# Revit family: Lighting-StreetLighting-GEWISS-STREET[O3]-WALL_BRACKET
name_source: partatom
category: Apparecchi per illuminazione
units: mm (PartAtom-declared; Revit-internal decimal feet)

## family parameters
Condiviso = No
Host = Superficie
Punto di calcolo locali = No
Quota connettore circolare = Usa diametro
Sorgente d'illuminazione = No
Taglio con vuoti quando caricato = No
Tipo di parte = Normale

## types (1)
- GW86167 - Galvanised steel - Grey
    Catalogue = LIGHTING
    Catalogue Range = STREET [O3]
    Colour = Graphite grey
    Description: = Wall-mounting bracket
    Descrizione = STREET WALL-MOUNTING BRACKET GR. GREY
    Dimensions AxBxC (mm) = 150x160x290
    EAN code = 8011564782518
    Electrocod = 240
    IDF = 5919c458-4529-45c8-8cfb-dc4348c4dfe2
    IDT = 734380e8-fd84-4dcf-8fb1-659ccad2240c
    Material = Galvanised steel
    Modello = GW86167
    Outer dim. LxHxD (mm) = 150x160x290
    Produttore = GEWISS S.p.A.
    Prospetto di default = 1219 mm
    SEO = Shelf
    Technical sheet = https://www.gewiss.com
    URL = https://www.gewiss.com
    Version file RFA = 19.4
    Weight (kg) = 1,6
    Weight (kg): = 1,6
